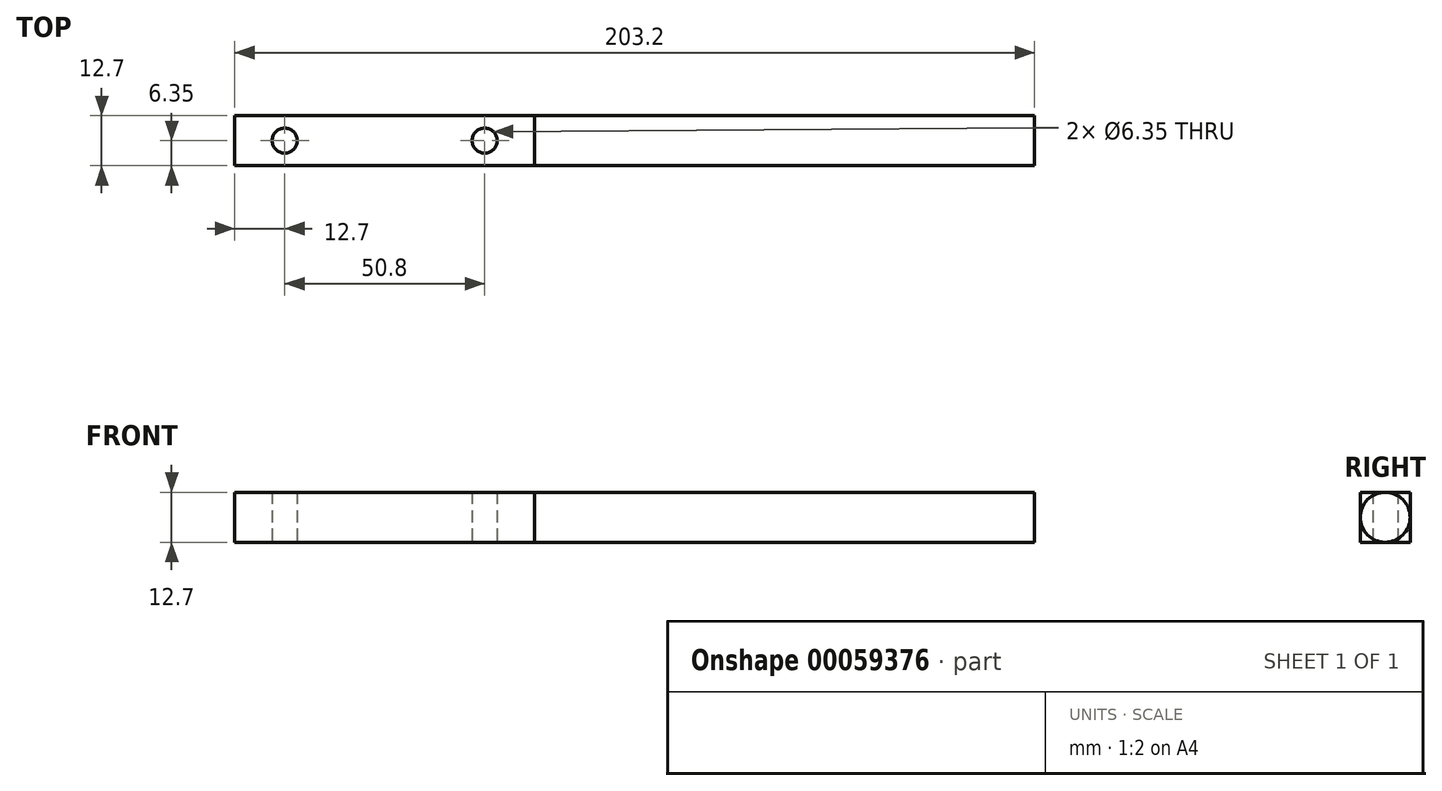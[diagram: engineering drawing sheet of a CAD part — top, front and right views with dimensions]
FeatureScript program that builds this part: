
annotation { "Feature Type Name" : "Feature", "Feature Type Description" : "" }
export const myFeature = defineFeature(function(context is Context, id is Id, definition is map)
    precondition{}
    {
        {
            var Q0;
            Q0=qCreatedBy(makeId("Top.planeOp"),FACE);
            var sketch = newSketch(context, id + "F0", { "sketchPlane" : qUnion([Q0])});
            skLineSegment(sketch, "E0", {"start": v(0, 0) * mm, "end": v(0, 6.35) * mm});
            skLineSegment(sketch, "E1", {"start": v(0, 6.35) * mm, "end": v(-76.2, 6.35) * mm});
            skLineSegment(sketch, "E2", {"start": v(-76.2, 6.35) * mm, "end": v(-76.2, -6.35) * mm});
            skLineSegment(sketch, "E3", {"start": v(-76.2, -6.35) * mm, "end": v(0, -6.35) * mm});
            skLineSegment(sketch, "E4", {"start": v(0, -6.35) * mm, "end": v(0, 0) * mm});
            skCircle(sketch, "E5", {"center": v(-63.5, 0) * mm, "radius": 3.18 * mm});
            skLineSegment(sketch, "E6.0", {"start": v(-12.7, 0) * mm, "end": v(-12.7, 6.35) * mm});
            skCircle(sketch, "E7", {"center": v(-12.7, 0) * mm, "radius": 3.18 * mm});
            skSolve(sketch);
        }
        {
            var Q0;
            {var subQ3=sQuery(id+"F0.wireOp",EDGE,"E0");Q0=makeQuery(id+"F0.imprint","IMPRINT",FACE,{"disambiguationData":[TD([[makeQuery(id+"F0.imprint","IMPRINT",EDGE,{"derivedFrom":subQ3}),1.0]])]});}
            extrude(context, id + "F1", {"entities" : qUnion([Q0]), "endBound" : BoundingType.SYMMETRIC, "depth" : 12.7 * mm});
        }
        {
            var Q0;
            Q0=makeQuery(id+"F1.opExtrude","SWEPT_FACE",FACE,{"disambiguationData":[OSD([sQuery(id+"F0.wireOp",EDGE,"E0"),sQuery(id+"F0.wireOp",EDGE,"E4")])]});
            var sketch = newSketch(context, id + "F2", { "sketchPlane" : qUnion([Q0])});
            skCircle(sketch, "E8", {"center": v(0, 0) * mm, "radius": 6.35 * mm});
            skSolve(sketch);
        }
        {
            var Q0;
            {var subQ0=sQuery(id+"F2.wireOp",EDGE,"E8");var subQ1=sQuery(id+"F0.wireOp",EDGE,"E4");var subQ2=sQuery(id+"F0.wireOp",EDGE,"E0");var subQ3=makeQuery(id+"F2.imprint","INTERSECT",VERTEX,{"derivedFrom":[makeQuery(id+"F1.opExtrude","CAP_EDGE",EDGE,{"disambiguationData":[OSD([subQ2,subQ1])],"isStart":false}),subQ0]});Q0=makeQuery(id+"F2.imprint","IMPRINT",FACE,{"disambiguationData":[TD([[makeQuery(id+"F2.imprint","IMPRINT",EDGE,{"disambiguationData":[TD([[subQ3,1.0]])],"derivedFrom":subQ0}),1.0]])]});}
            extrude(context, id + "F3", {"entities" : qUnion([Q0]), "operationType" : NewBodyOperationType.ADD, "depth" : 127 * mm});
        }
    });
